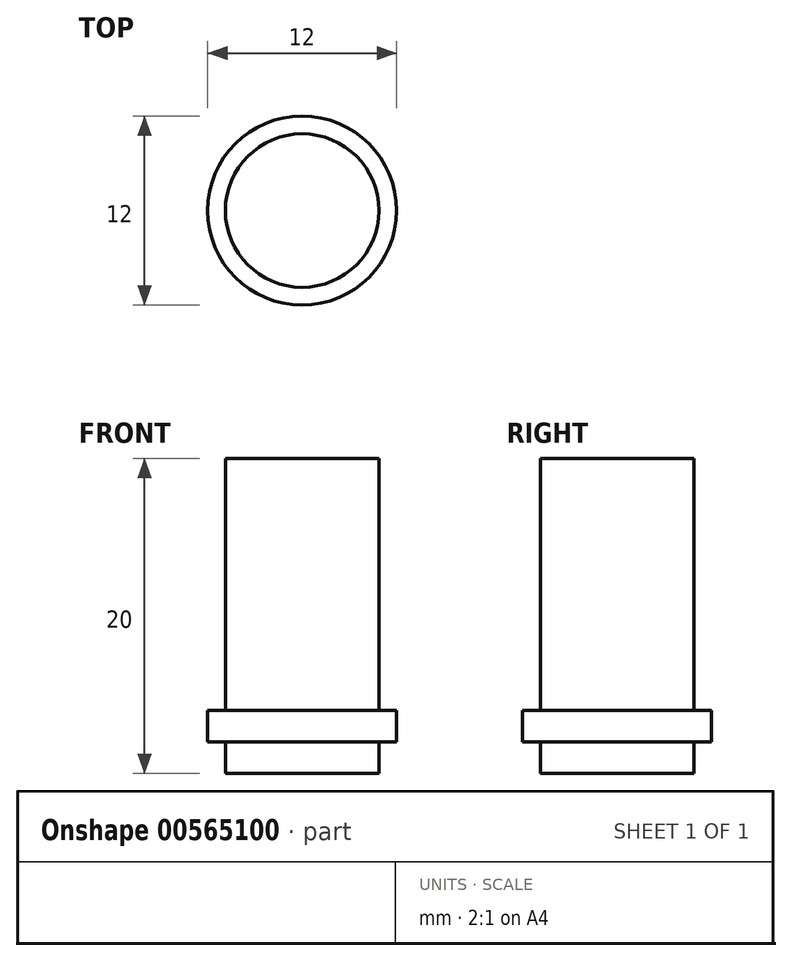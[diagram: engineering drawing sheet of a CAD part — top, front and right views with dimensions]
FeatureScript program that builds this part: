
annotation { "Feature Type Name" : "Feature", "Feature Type Description" : "" }
export const myFeature = defineFeature(function(context is Context, id is Id, definition is map)
    precondition{}
    {
        {
            var Q0;
            Q0=qCreatedBy(makeId("Top.planeOp"),FACE);
            var sketch = newSketch(context, id + "F0", { "sketchPlane" : qUnion([Q0])});
            skCircle(sketch, "E0", {"center": v(0, 0) * mm, "radius": 4.88 * mm});
            skCircle(sketch, "E1", {"center": v(0, 0) * mm, "radius": 6 * mm});
            skSolve(sketch);
        }
        {
            var Q0;
            Q0=makeQuery(id+"F0.imprint","IMPRINT",FACE,{"disambiguationData":[TD([[makeQuery(id+"F0.imprint","IMPRINT",EDGE,{"derivedFrom":sQuery(id+"F0.wireOp",EDGE,"E0")}),1.0]])]});
            extrude(context, id + "F1", {"entities" : qUnion([Q0]), "depth" : 20 * mm, "offsetDistance" : 25 * mm});
        }
        {
            var Q0;
            Q0=makeQuery(id+"F0.imprint","IMPRINT",FACE,{"disambiguationData":[TD([[makeQuery(id+"F0.imprint","IMPRINT",EDGE,{"derivedFrom":sQuery(id+"F0.wireOp",EDGE,"E0")}),-1.0]])]});
            extrude(context, id + "F2", {"entities" : qUnion([Q0]), "operationType" : NewBodyOperationType.ADD, "depth" : 4 * mm, "offsetDistance" : 25 * mm, "hasSecondDirection" : true, "secondDirectionOppositeDirection" : false, "secondDirectionDepth" : 2 * mm});
        }
    });
